# Revit family: TMI - W2252 - Wall_Combo_2 Doors_Open1
name_source: partatom
category: Casework
revit_build: Autodesk Revit 2016 (Build: 20150220_1215(x64)
units: mm (PartAtom-declared; Revit-internal decimal feet)

## family parameters
Cut with Voids When Loaded = No
Host = Face
OmniClass Number = 23.40.35.14.11
OmniClass Title = Modular Casework
Room Calculation Point = No
Shared = No

## types (5) — shared parameters
Cabinet Finish = Plastic Laminate
Casework Back Thickness = 1/4"
Casework Thickness = 3/4"
Center Gap = 1/8"
Default Elevation = 84"
Depth = 14"
Description = Wall, Combo, 2 Doors, Open
Distance of Door from Top of Casework = 1/4"
Distance of Hinge from Edge of Casework = 1 13/32"
Door Thickness = 3/4"
Height = 30"
Interior Finish = <By Category>
Manufacturer = TMI Systems Corporation
Model = W2252
Shelf Thickness = 3/4"
URL = www.tmisystems.com

## per-type parameters (varying)
| type | Width |
| 24" x 30" x 14" | 24" |
| 27" x 30" x 14" | 27" |
| 30" x 30" x 14" | 30" |
| 33" x 30" x 14" | 33" |
| 36" x 30" x 14" | 36" |

## geometry (parser evidence)
native form markers: Blend x2, Sweep x10
no freeform markers — native parametric forms only
